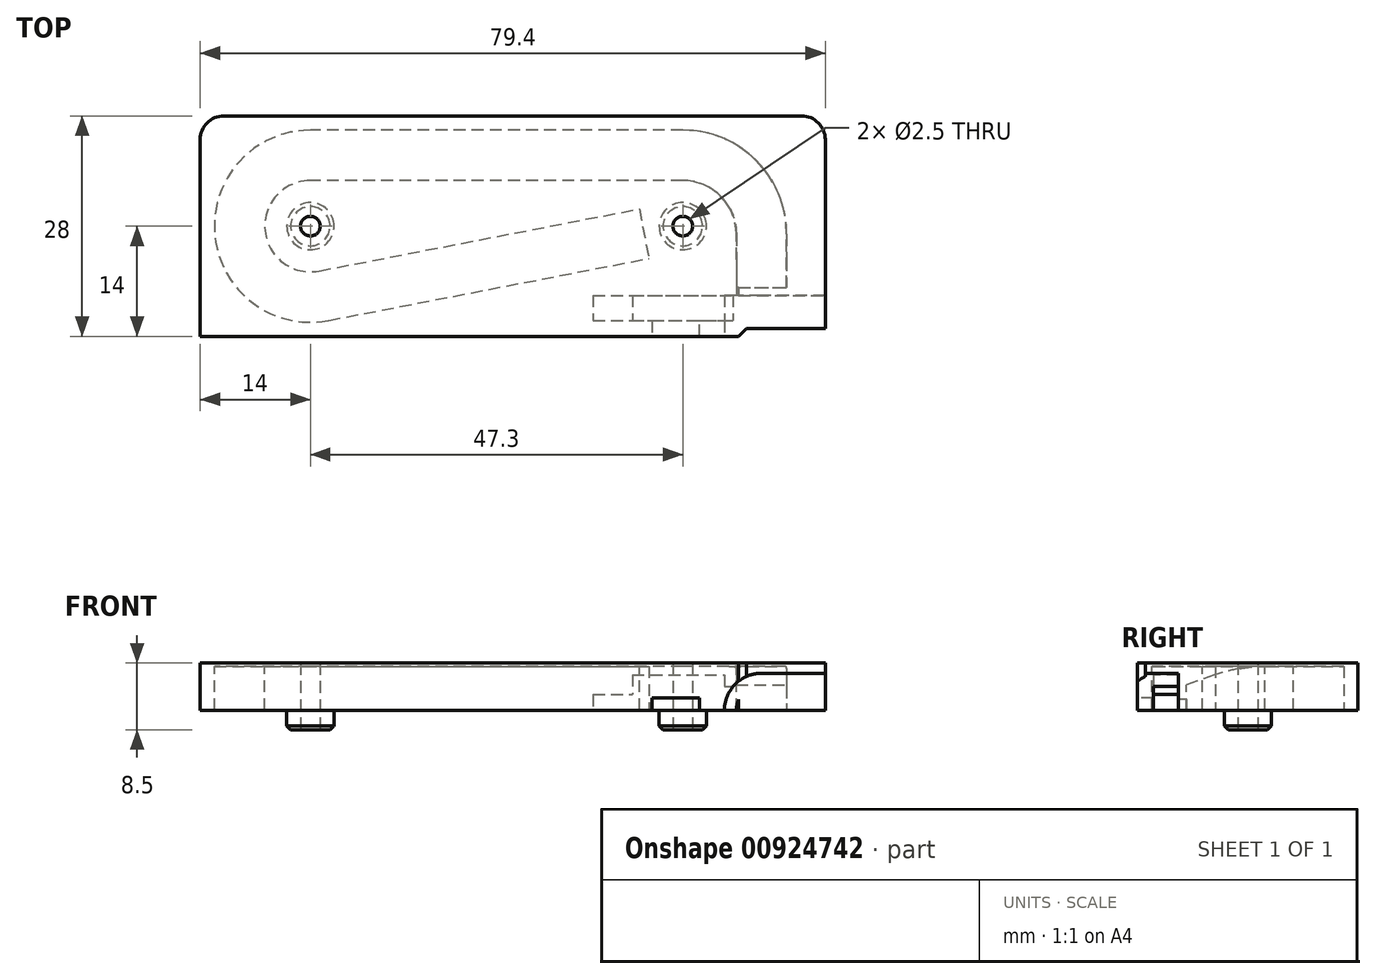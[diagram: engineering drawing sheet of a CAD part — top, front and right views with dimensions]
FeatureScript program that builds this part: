
annotation { "Feature Type Name" : "Feature", "Feature Type Description" : "" }
export const myFeature = defineFeature(function(context is Context, id is Id, definition is map)
    precondition{}
    {
        {
            var Q0;
            Q0=qCreatedBy(makeId("Top.planeOp"),FACE);
            var sketch = newSketch(context, id + "F0", { "sketchPlane" : qUnion([Q0])});
            skLineSegment(sketch, "E0.bottom", {"start": v(-71.3, -6.2) * mm, "end": v(8.1, -6.2) * mm});
            skLineSegment(sketch, "E0.top", {"start": v(-71.3, 21.8) * mm, "end": v(8.1, 21.8) * mm});
            skLineSegment(sketch, "E0.left", {"start": v(-71.3, -6.2) * mm, "end": v(-71.3, 21.8) * mm});
            skLineSegment(sketch, "E0.right", {"start": v(8.1, -6.2) * mm, "end": v(8.1, 21.8) * mm});
            skLineSegment(sketch, "E1", {"start": v(0, 0) * mm, "end": v(0, 6.8) * mm});
            skLineSegment(sketch, "E2", {"start": v(-10, 16.8) * mm, "end": v(-57.3, 16.8) * mm});
            skLineSegment(sketch, "E3", {"start": v(-55.59, -1.04) * mm, "end": v(-14.9, 6.85) * mm});
            skPoint(sketch, "E4.visualSharp", {"position": v(0, 16.8) * mm});
            skArc(sketch, "E4.filletArc", {"start": v(0, 6.8) * mm, "mid": v(-2.93, 13.87) * mm, "end": v(-10, 16.8) * mm});
            skLineSegment(sketch, "E5", {"start": v(0, 0) * mm, "end": v(0, -6.2) * mm});
            skCircle(sketch, "E6", {"center": v(-57.3, 7.8) * mm, "radius": 3 * mm});
            skPoint(sketch, "E6.centerSnap0", {"position": v(-71.3, 7.8) * mm});
            skCircle(sketch, "E7", {"center": v(-10, 7.8) * mm, "radius": 3 * mm});
            skPoint(sketch, "E7.centerSnap0", {"position": v(8.1, 7.8) * mm});
            skCircle(sketch, "E8", {"center": v(-57.3, 7.8) * mm, "radius": 1.25 * mm});
            skCircle(sketch, "E9", {"center": v(-10, 7.8) * mm, "radius": 1.25 * mm});
            skArc(sketch, "E10", {"start": v(-57.3, 16.8) * mm, "mid": v(-66.26, 6.94) * mm, "end": v(-55.59, -1.04) * mm});
            skLineSegment(sketch, "E11", {"start": v(8.1, -5.2) * mm, "end": v(-1.9, -5.2) * mm});
            skLineSegment(sketch, "E12", {"start": v(-1.9, -5.2) * mm, "end": v(-2.9, -6.2) * mm});
            skSolve(sketch);
        }
        {
            var Q0;
            Q0=makeQuery(id+"F0.imprint","IMPRINT",FACE,{"disambiguationData":[TD([[makeQuery(id+"F0.imprint","IMPRINT",EDGE,{"derivedFrom":sQuery(id+"F0.wireOp",EDGE,"7f5f69c7-28f1-4018-8948-6ec0e1df88dc.0")}),-1.0]])]});
            var Q1;
            {var subQ1=sQuery(id+"F0.wireOp",EDGE,"E0.top");Q1=makeQuery(id+"F0.imprint","IMPRINT",FACE,{"disambiguationData":[TD([[makeQuery(id+"F0.imprint","IMPRINT",EDGE,{"derivedFrom":subQ1}),-1.0]])]});}
            var Q2;
            Q2=makeQuery(id+"F0.imprint","IMPRINT",FACE,{"disambiguationData":[TD([[makeQuery(id+"F0.imprint","IMPRINT",EDGE,{"derivedFrom":sQuery(id+"F0.wireOp",EDGE,"E6")}),1.0]])]});
            var Q3;
            Q3=makeQuery(id+"F0.imprint","IMPRINT",FACE,{"disambiguationData":[TD([[makeQuery(id+"F0.imprint","IMPRINT",EDGE,{"derivedFrom":sQuery(id+"F0.wireOp",EDGE,"E7")}),1.0]])]});
            extrude(context, id + "F1", {"entities" : qUnion([Q0, Q1, Q2, Q3]), "depth" : 13 * mm, "offsetDistance" : 25 * mm});
        }
        {
            var Q0;
            Q0=makeQuery(id+"F0.imprint","IMPRINT",FACE,{"disambiguationData":[TD([[makeQuery(id+"F0.imprint","IMPRINT",EDGE,{"derivedFrom":sQuery(id+"F0.wireOp",EDGE,"E6")}),1.0]])]});
            var Q1;
            Q1=makeQuery(id+"F0.imprint","IMPRINT",FACE,{"disambiguationData":[TD([[makeQuery(id+"F0.imprint","IMPRINT",EDGE,{"derivedFrom":sQuery(id+"F0.wireOp",EDGE,"E7")}),1.0]])]});
            extrude(context, id + "F2", {"entities" : qUnion([Q0, Q1]), "operationType" : NewBodyOperationType.ADD, "oppositeDirection" : true, "depth" : 2.5 * mm, "offsetDistance" : 25 * mm});
        }
        {
            var Q0;
            Q0=makeQuery(id+"F2.opExtrude","CAP_EDGE",EDGE,{"disambiguationData":[OSD([sQuery(id+"F0.wireOp",EDGE,"E6")])],"isStart":false});
            var Q1;
            Q1=makeQuery(id+"F2.opExtrude","CAP_EDGE",EDGE,{"disambiguationData":[OSD([sQuery(id+"F0.wireOp",EDGE,"E7")])],"isStart":false});
            chamfer(context, id + "F3", {"entities" : qUnion([Q0, Q1]), "width" : 0.5 * mm, "tangentPropagation" : true});
        }
        {
            var Q0;
            Q0=makeQuery(id+"F1.opExtrude","CAP_FACE",FACE,{"disambiguationData":[OSD([sQuery(id+"F0.wireOp",EDGE,"E0.bottom"),sQuery(id+"F0.wireOp",EDGE,"E0.top"),sQuery(id+"F0.wireOp",EDGE,"E0.left"),sQuery(id+"F0.wireOp",EDGE,"E0.right"),sQuery(id+"F0.wireOp",EDGE,"E8"),sQuery(id+"F0.wireOp",EDGE,"E9")])],"isStart":false});
            var sketch = newSketch(context, id + "F4", { "sketchPlane" : qUnion([Q0])});
            skCircle(sketch, "E13.0", {"center": v(-10, 7.8) * mm, "radius": 3 * mm});
            skCircle(sketch, "E13.1", {"center": v(-57.3, 7.8) * mm, "radius": 3 * mm});
            skSolve(sketch);
        }
        {
            var Q0;
            Q0=qCreatedBy(makeId("Front.planeOp"),FACE);
            var Q1;
            Q1=sQuery(id+"F0.wireOp",VERTEX,"E1.end");
            cPlane(context, id + "F5", {"entities" : qUnion([Q0, Q1]), "cplaneType" : CPlaneType.PLANE_POINT, "offset" : 25 * mm, "width" : 150 * mm, "height" : 150 * mm});
        }
        {
            var Q0;
            Q0=qCreatedBy(id+"F5.planeOp",FACE);
            var sketch = newSketch(context, id + "F6", { "sketchPlane" : qUnion([Q0])});
            skLineSegment(sketch, "E14", {"start": v(-3.2, 0) * mm, "end": v(3.2, 0) * mm});
            skLineSegment(sketch, "E15", {"start": v(-3.2, 0) * mm, "end": v(-3.2, 2.4) * mm});
            skLineSegment(sketch, "E16", {"start": v(3.2, 2.4) * mm, "end": v(3.2, 0) * mm});
            skArc(sketch, "E17", {"start": v(3.2, 2.4) * mm, "mid": v(0, 5.6) * mm, "end": v(-3.2, 2.4) * mm});
            skLineSegment(sketch, "E18", {"start": v(-3.2, 2.4) * mm, "end": v(-3.2, 5.6) * mm});
            skPoint(sketch, "E18.endSnap0", {"position": v(0, 5.6) * mm});
            skLineSegment(sketch, "E19", {"start": v(-3.2, 5.6) * mm, "end": v(3.2, 5.6) * mm});
            skLineSegment(sketch, "E20", {"start": v(3.2, 5.6) * mm, "end": v(3.2, 2.4) * mm});
            skSolve(sketch);
        }
        {
            var Q0;
            Q0=qCreatedBy(makeId("Right.planeOp"),FACE);
            var sketch = newSketch(context, id + "F7", { "sketchPlane" : qUnion([Q0])});
            skLineSegment(sketch, "E21", {"start": v(6.8, 0) * mm, "end": v(0, -2.4) * mm});
            skSolve(sketch);
        }
        {
            var Q0;
            Q0 = qSketchRegion(id + "F6", true);
            var Q1;
            Q1=sQuery(id+"F0.wireOp",EDGE,"E4.filletArc");
            var Q2;
            Q2=sQuery(id+"F0.wireOp",EDGE,"E2");
            var Q3;
            Q3=sQuery(id+"F0.wireOp",EDGE,"d1730343-6995-424f-9b53-40ab9ed45578.filletArc");
            var Q4;
            Q4=sQuery(id+"F0.wireOp",EDGE,"4a9f4d60-a468-4d21-9085-bbe88fbe73fb.filletArc");
            var Q5;
            Q5=sQuery(id+"F0.wireOp",EDGE,"s2Idn5qi-RAJ9-igUd-Ia3V-9sphePnUOk5o");
            var Q6;
            Q6=sQuery(id+"F0.wireOp",EDGE,"E10");
            var Q7;
            Q7=sQuery(id+"F0.wireOp",EDGE,"E3");
            sweep(context, id + "F8", {"operationType" : NewBodyOperationType.REMOVE, "profiles" : qUnion([Q0]), "path" : qUnion([Q1, Q2, Q3, Q4, Q5, Q6, Q7])});
        }
        {
            var Q0;
            Q0 = qSketchRegion(id + "F6", true);
            var Q1;
            Q1=sQuery(id+"F7.wireOp",EDGE,"E21");
            sweep(context, id + "F9", {"operationType" : NewBodyOperationType.REMOVE, "profiles" : qUnion([Q0]), "path" : qUnion([Q1])});
        }
        {
            var Q0;
            {var subQ0=sQuery(id+"F6.wireOp",EDGE,"94ECcUXc-tZfw-cjEn-tCD6-P7DTjVil75Tr");Q0=makeQuery(id+"F9.boolean.opBoolean","MERGE",EDGE,{"derivedFrom":[makeQuery(id+"F8.boolean.opBoolean","COPY",EDGE,{"derivedFrom":makeQuery(id+"F8.opSweep","CAP_EDGE",EDGE,{"disambiguationData":[OSD([sQuery(id+"F0.wireOp",VERTEX,"E4.filletArc.start"),subQ0])],"isStart":true})})],"fromTools":[makeQuery(id+"F9.opSweep","CAP_EDGE",EDGE,{"disambiguationData":[OSD([subQ0,sQuery(id+"F7.wireOp",VERTEX,"iZJ95Zzg-F8Eo-B6av-DNtS-iHiygdJsTgDz.start")])],"isStart":true})]});}
            var Q1;
            {var subQ0=sQuery(id+"F6.wireOp",EDGE,"OD5Wdmzi-xWeJ-Cclx-zYLs-QJslX0R6a0eT");Q1=makeQuery(id+"F9.boolean.opBoolean","MERGE",EDGE,{"derivedFrom":[makeQuery(id+"F8.boolean.opBoolean","COPY",EDGE,{"derivedFrom":makeQuery(id+"F8.opSweep","CAP_EDGE",EDGE,{"disambiguationData":[OSD([sQuery(id+"F0.wireOp",VERTEX,"E4.filletArc.start"),subQ0])],"isStart":true})})],"fromTools":[makeQuery(id+"F9.opSweep","CAP_EDGE",EDGE,{"disambiguationData":[OSD([subQ0,sQuery(id+"F7.wireOp",VERTEX,"iZJ95Zzg-F8Eo-B6av-DNtS-iHiygdJsTgDz.start")])],"isStart":true})]});}
            var Q2;
            {var subQ0=sQuery(id+"F6.wireOp",EDGE,"sauD6JAj-hWHt-r4tU-MFAL-XhgwlfRS9sgR");Q2=makeQuery(id+"F9.boolean.opBoolean","MERGE",EDGE,{"derivedFrom":[makeQuery(id+"F8.boolean.opBoolean","COPY",EDGE,{"derivedFrom":makeQuery(id+"F8.opSweep","CAP_EDGE",EDGE,{"disambiguationData":[OSD([sQuery(id+"F0.wireOp",VERTEX,"E4.filletArc.start"),subQ0])],"isStart":true})})],"fromTools":[makeQuery(id+"F9.opSweep","CAP_EDGE",EDGE,{"disambiguationData":[OSD([subQ0,sQuery(id+"F7.wireOp",VERTEX,"iZJ95Zzg-F8Eo-B6av-DNtS-iHiygdJsTgDz.start")])],"isStart":true})]});}
            fillet(context, id + "F10", {"entities" : qUnion([Q0, Q1, Q2]), "radius" : 20 * mm, "tangentPropagation" : true, "allowEdgeOverflow" : false});
        }
        {
            var Q0;
            Q0=makeQuery(id+"F1.opExtrude","SWEPT_FACE",FACE,{"disambiguationData":[OSD([sQuery(id+"F0.wireOp",EDGE,"E0.bottom")])]});
            var sketch = newSketch(context, id + "F11", { "sketchPlane" : qUnion([Q0])});
            skArc(sketch, "E22", {"start": v(0, 4.7) * mm, "mid": v(-3.32, 3.32) * mm, "end": v(-4.7, 0) * mm});
            skCircle(sketch, "E23", {"center": v(0, 0) * mm, "radius": 3.2 * mm});
            skLineSegment(sketch, "E24", {"start": v(8.1, 0) * mm, "end": v(-4.7, 0) * mm});
            skLineSegment(sketch, "E25", {"start": v(8.1, 0) * mm, "end": v(8.1, 4.7) * mm});
            skLineSegment(sketch, "E26", {"start": v(8.1, 4.7) * mm, "end": v(0, 4.7) * mm});
            skSolve(sketch);
        }
        {
            var Q0;
            Q0 = qSketchRegion(id + "F11", true);
            extrude(context, id + "F12", {"entities" : qUnion([Q0]), "operationType" : NewBodyOperationType.REMOVE, "oppositeDirection" : true, "depth" : 5.2 * mm, "offsetDistance" : 25 * mm});
        }
        {
            var Q0;
            {var subQ0=sQuery(id+"F11.wireOp",EDGE,"E24");var subQ1=sQuery(id+"F11.wireOp",EDGE,"E23");var subQ2=makeQuery(id+"F11.imprint","INTERSECT",VERTEX,{"disambiguationData":[OD(0.0)],"derivedFrom":[subQ1,subQ0]});Q0=makeQuery(id+"F11.imprint","IMPRINT",FACE,{"disambiguationData":[TD([[makeQuery(id+"F11.imprint","IMPRINT",EDGE,{"disambiguationData":[TD([[subQ2,1.0]])],"derivedFrom":subQ1}),1.0]])]});}
            var Q1;
            {var subQ0=sQuery(id+"F11.wireOp",EDGE,"E24");var subQ1=sQuery(id+"F11.wireOp",EDGE,"E23");var subQ2=makeQuery(id+"F11.imprint","INTERSECT",VERTEX,{"disambiguationData":[OD(0.0)],"derivedFrom":[subQ1,subQ0]});Q1=makeQuery(id+"F11.imprint","IMPRINT",FACE,{"disambiguationData":[TD([[makeQuery(id+"F11.imprint","IMPRINT",EDGE,{"disambiguationData":[TD([[subQ2,-1.0]])],"derivedFrom":subQ1}),1.0]])]});}
            var Q2;
            {var subQ0=sQuery(id+"F11.wireOp",EDGE,"E24");var subQ1=sQuery(id+"F11.wireOp",EDGE,"E23");var subQ2=makeQuery(id+"F11.imprint","INTERSECT",VERTEX,{"disambiguationData":[OD(1.0)],"derivedFrom":[subQ1,subQ0]});Q2=makeQuery(id+"F11.imprint","IMPRINT",FACE,{"disambiguationData":[TD([[makeQuery(id+"F11.imprint","IMPRINT",EDGE,{"disambiguationData":[TD([[subQ2,1.0]])],"derivedFrom":subQ1}),1.0]])]});}
            var Q3;
            Q3=makeQuery(id+"F9.boolean.opBoolean","COPY",FACE,{"derivedFrom":makeQuery(id+"F9.opSweep","CAP_FACE",FACE,{"disambiguationData":[OSD([sQuery(id+"F6.wireOp",EDGE,"E14"),sQuery(id+"F6.wireOp",EDGE,"sauD6JAj-hWHt-r4tU-MFAL-XhgwlfRS9sgR"),sQuery(id+"F6.wireOp",EDGE,"OD5Wdmzi-xWeJ-Cclx-zYLs-QJslX0R6a0eT"),sQuery(id+"F6.wireOp",EDGE,"94ECcUXc-tZfw-cjEn-tCD6-P7DTjVil75Tr"),sQuery(id+"F7.wireOp",VERTEX,"iZJ95Zzg-F8Eo-B6av-DNtS-iHiygdJsTgDz.end")])],"isStart":false})});
            extrude(context, id + "F13", {"entities" : qUnion([Q0, Q1, Q2]), "operationType" : NewBodyOperationType.REMOVE, "endBound" : BoundingType.UP_TO_SURFACE, "oppositeDirection" : true, "depth" : 7 * mm, "endBoundEntityFace" : qUnion([Q3]), "offsetDistance" : 25 * mm});
        }
        {
            var Q0;
            Q0=qCreatedBy(makeId("Top.planeOp"),FACE);
            var sketch = newSketch(context, id + "F14", { "sketchPlane" : qUnion([Q0])});
            skLineSegment(sketch, "E27.bottom", {"start": v(-21.4, -1) * mm, "end": v(-4.7, -1) * mm});
            skLineSegment(sketch, "E27.top", {"start": v(-21.4, -4.2) * mm, "end": v(-4.7, -4.2) * mm});
            skLineSegment(sketch, "E27.left", {"start": v(-21.4, -1) * mm, "end": v(-21.4, -4.2) * mm});
            skLineSegment(sketch, "E27.right", {"start": v(-4.7, -1) * mm, "end": v(-4.7, -4.2) * mm});
            skLineSegment(sketch, "E28", {"start": v(-16.4, -1) * mm, "end": v(-16.4, -4.2) * mm});
            skLineSegment(sketch, "E29", {"start": v(-13.9, -4.2) * mm, "end": v(-13.9, -6.2) * mm});
            skLineSegment(sketch, "E30", {"start": v(-13.9, -6.2) * mm, "end": v(-7.9, -6.2) * mm});
            skLineSegment(sketch, "E31", {"start": v(-7.9, -6.2) * mm, "end": v(-7.9, -4.2) * mm});
            skLineSegment(sketch, "E32", {"start": v(-4.7, -4.2) * mm, "end": v(-2.7, -4.2) * mm});
            skLineSegment(sketch, "E33", {"start": v(-2.7, -4.2) * mm, "end": v(-2.7, -1) * mm});
            skLineSegment(sketch, "E34", {"start": v(-2.7, -1) * mm, "end": v(-4.7, -1) * mm});
            skSolve(sketch);
        }
        {
            var Q0;
            {var subQ0=sQuery(id+"F14.wireOp",EDGE,"E27.left");Q0=makeQuery(id+"F14.imprint","IMPRINT",FACE,{"disambiguationData":[TD([[makeQuery(id+"F14.imprint","IMPRINT",EDGE,{"derivedFrom":subQ0}),1.0]])]});}
            extrude(context, id + "F15", {"entities" : qUnion([Q0]), "operationType" : NewBodyOperationType.REMOVE, "depth" : 2 * mm, "offsetDistance" : 25 * mm});
        }
        {
            var Q0;
            {var subQ0=sQuery(id+"F14.wireOp",EDGE,"E27.right");Q0=makeQuery(id+"F14.imprint","IMPRINT",FACE,{"disambiguationData":[TD([[makeQuery(id+"F14.imprint","IMPRINT",EDGE,{"derivedFrom":subQ0}),-1.0]])]});}
            extrude(context, id + "F16", {"entities" : qUnion([Q0]), "operationType" : NewBodyOperationType.REMOVE, "depth" : 4.5 * mm, "offsetDistance" : 25 * mm});
        }
        {
            var Q0;
            {var subQ0=sQuery(id+"F14.wireOp",EDGE,"E29");Q0=makeQuery(id+"F14.imprint","IMPRINT",FACE,{"disambiguationData":[TD([[makeQuery(id+"F14.imprint","IMPRINT",EDGE,{"derivedFrom":subQ0}),1.0]])]});}
            extrude(context, id + "F17", {"entities" : qUnion([Q0]), "operationType" : NewBodyOperationType.REMOVE, "surfaceOperationType" : NewSurfaceOperationType.ADD, "depth" : 1.6 * mm, "offsetDistance" : 25 * mm});
        }
        {
            var Q0;
            Q0=makeQuery(id+"F14.imprint","IMPRINT",FACE,{"disambiguationData":[TD([[makeQuery(id+"F14.imprint","IMPRINT",EDGE,{"derivedFrom":sQuery(id+"F14.wireOp",EDGE,"E27.right")}),1.0]])]});
            extrude(context, id + "F18", {"entities" : qUnion([Q0]), "operationType" : NewBodyOperationType.REMOVE, "depth" : 3 * mm, "offsetDistance" : 25 * mm});
        }
        {
            var Q0;
            Q0=makeQuery(id+"F1.opExtrude","CAP_EDGE",EDGE,{"disambiguationData":[OSD([sQuery(id+"F0.wireOp",EDGE,"E0.right")])],"isStart":false});
            var Q1;
            Q1=makeQuery(id+"F1.opExtrude","CAP_EDGE",EDGE,{"disambiguationData":[OSD([sQuery(id+"F0.wireOp",EDGE,"E0.top")])],"isStart":false});
            var Q2;
            Q2=makeQuery(id+"F1.opExtrude","CAP_EDGE",EDGE,{"disambiguationData":[OSD([sQuery(id+"F0.wireOp",EDGE,"E0.left")])],"isStart":false});
            var Q3;
            Q3=makeQuery(id+"F1.opExtrude","SWEPT_EDGE",EDGE,{"disambiguationData":[OSD([sQuery(id+"F0.wireOp",EDGE,"E0.top"),sQuery(id+"F0.wireOp",EDGE,"E0.left")])]});
            var Q4;
            Q4=makeQuery(id+"F1.opExtrude","SWEPT_EDGE",EDGE,{"disambiguationData":[OSD([sQuery(id+"F0.wireOp",EDGE,"E0.top"),sQuery(id+"F0.wireOp",EDGE,"E0.right")])]});
            fillet(context, id + "F19", {"entities" : qUnion([Q0, Q1, Q2, Q3, Q4]), "radius" : 3 * mm, "tangentPropagation" : true, "allowEdgeOverflow" : false});
        }
        {
            var Q0;
            Q0=makeQuery(id+"F4.imprint","IMPRINT",FACE,{"disambiguationData":[TD([[makeQuery(id+"F4.imprint","IMPRINT",EDGE,{"derivedFrom":sQuery(id+"F4.wireOp",EDGE,"E13.0")}),-1.0]])]});
            var sketch = newSketch(context, id + "F20", { "sketchPlane" : qUnion([Q0])});
            skLineSegment(sketch, "E35.bottom", {"start": v(30.79, -31.2) * mm, "end": v(-82.66, -31.2) * mm});
            skLineSegment(sketch, "E35.top", {"start": v(30.79, 40.77) * mm, "end": v(-82.66, 40.77) * mm});
            skLineSegment(sketch, "E35.left", {"start": v(30.79, -31.2) * mm, "end": v(30.79, 40.77) * mm});
            skLineSegment(sketch, "E35.right", {"start": v(-82.66, -31.2) * mm, "end": v(-82.66, 40.77) * mm});
            skSolve(sketch);
        }
        {
            var Q0;
            Q0 = qSketchRegion(id + "F20", true);
            extrude(context, id + "F21", {"entities" : qUnion([Q0]), "operationType" : NewBodyOperationType.REMOVE, "oppositeDirection" : true, "depth" : 7 * mm, "offsetDistance" : 25 * mm});
        }
    });
